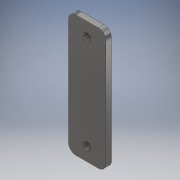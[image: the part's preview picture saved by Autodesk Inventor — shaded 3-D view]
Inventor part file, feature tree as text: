
AUTODESK INVENTOR PART (.ipt)
format: ipt  version: 2018 (Build 220112000, 112)  size: 118,784 bytes
history: native  units: mm
features: extrude x2, sketch x2, fillet x1
ambient origin geometry x8: Origin, YZ Plane, XZ Plane, XY Plane, X Axis, Y Axis, Z Axis, Center Point
bodies: Body1 (feature_tree)
feature tree (5):
  extrude  "Extrusión3"  Depth=40.0mm
  extrude  "Extrusión4"  Depth=8.0mm
  fillet  "Empalme2"  Radius=8.0mm
  sketch  "Boceto3"  dims[d15=6.0mm d16=40.0mm]
  sketch  "Boceto4"  dims[d17=130.0mm d18=0.0mm d19=75.0mm d20=8.0mm d21=26.0mm d22=100.0mm d23=0.0mm d24=8.0mm]
